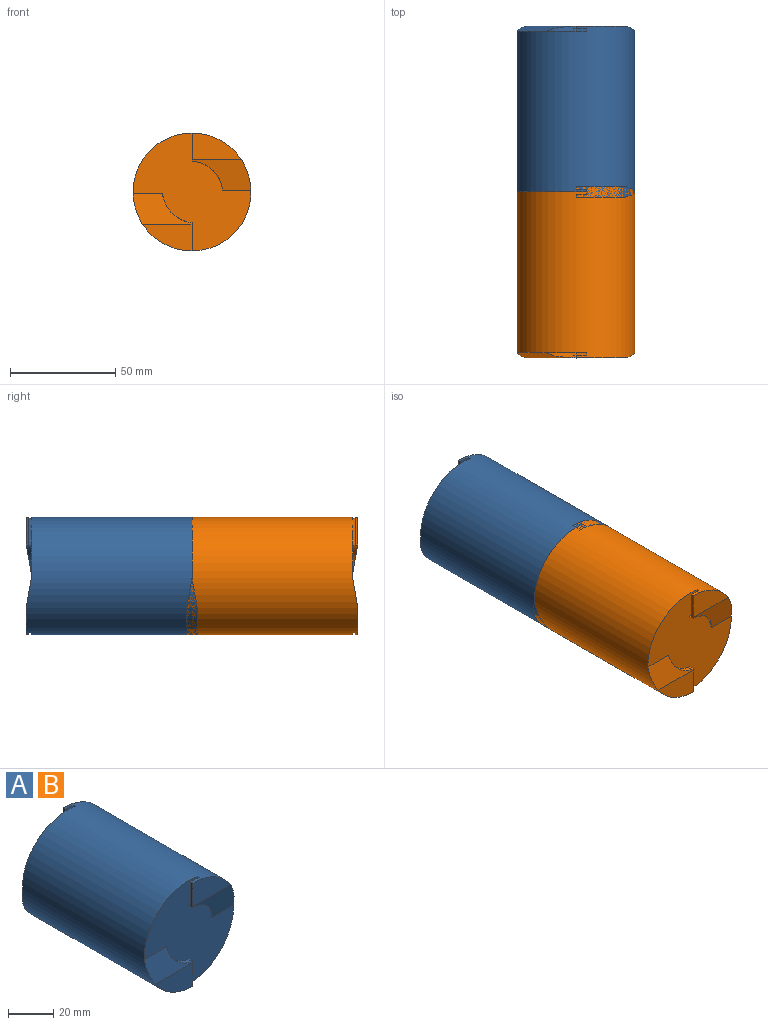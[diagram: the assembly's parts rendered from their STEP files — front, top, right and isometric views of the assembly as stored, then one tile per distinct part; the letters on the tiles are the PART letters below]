
ASSEMBLY  parts=2 mates=1
PART A: 31 faces, bbox 55.9x81.3x55.9 mm
  f0: plane 13.39x1.33mm, normal (1,0,0), area 17.7mm2, adj f1,f6,f7,f9,f14
  f1: cylinder r=27.97mm len=81.28mm, axis (0,1,0), area 13724mm2, adj f0,f2,f3,f5,f7,f8,f9,f10
  f2: plane 13.39x1.27mm, normal (-1,0,0), area 17mm2, adj f1,f4,f5,f8,f11
  f3: plane 55.95x55.95mm, normal (0,-1,0), area 1735.2mm2, adj f1,f4,f6,f8,f9,f10,f12,f13
  f4: cylinder r=15.37mm len=14.52mm, axis (0,1,0), area 33.2mm2, adj f2,f3,f8,f12
  f5: plane 23.46x12.73mm, normal (0,-1,0), area 210.4mm2, adj f1,f2,f8
  f6: cylinder r=15.76mm len=14.01mm, axis (0,1,0), area 31.7mm2, adj f0,f3,f9,f15
  f7: plane 23.46x12.73mm, normal (0,-1,0), area 210.4mm2, adj f0,f1,f9
  f8: plane 27.96x14.41mm, normal (0,-0.98,-0.17), area 233.9mm2, adj f1,f2,f3,f4,f5
  f9: plane 27.96x14.41mm, normal (0,-0.98,0.17), area 242.2mm2, adj f0,f1,f3,f6,f7
  f10: plane 12.92x1.27mm, normal (-1,0,0), area 16.4mm2, adj f1,f3,f11,f12
  f11: plane 13.39x5.08mm, normal (0,1,0), area 67.2mm2, adj f1,f2,f10,f12
  f12: plane 5.08x1.27mm, normal (0,0,1), area 6.5mm2, adj f3,f4,f10,f11
  f13: plane 12.33x1.21mm, normal (1,0,0), area 14.9mm2, adj f1,f3,f14,f15
  f14: plane 13.39x7.62mm, normal (0,1,0), area 99.3mm2, adj f0,f1,f13,f15
  f15: plane 7.62x1.21mm, normal (0,0,-1), area 9.2mm2, adj f3,f6,f13,f14
  f16: plane 13.39x1.33mm, normal (1,0,0), area 17.7mm2, adj f1,f21,f22,f24,f29
  f17: plane 13.39x1.27mm, normal (-1,0,0), area 17mm2, adj f1,f19,f20,f23,f26
  f18: plane 55.95x55.95mm, normal (0,1,0), area 1735.2mm2, adj f1,f19,f21,f23,f24,f25,f27,f28
  f19: cylinder r=15.37mm len=14.52mm, axis (0,-1,0), area 33.2mm2, adj f17,f18,f23,f27
  f20: plane 23.46x12.73mm, normal (0,1,0), area 210.4mm2, adj f1,f17,f23
  f21: cylinder r=15.76mm len=14.01mm, axis (0,-1,0), area 31.7mm2, adj f16,f18,f24,f30
  f22: plane 23.46x12.73mm, normal (0,1,0), area 210.4mm2, adj f1,f16,f24
  f23: plane 27.96x14.41mm, normal (0,0.98,-0.17), area 233.9mm2, adj f1,f17,f18,f19,f20
  f24: plane 27.96x14.41mm, normal (0,0.98,0.17), area 242.2mm2, adj f1,f16,f18,f21,f22
  f25: plane 12.92x1.27mm, normal (-1,0,0), area 16.4mm2, adj f1,f18,f26,f27
  f26: plane 13.39x5.08mm, normal (0,-1,0), area 67.2mm2, adj f1,f17,f25,f27
  f27: plane 5.08x1.27mm, normal (0,0,1), area 6.5mm2, adj f18,f19,f25,f26
  f28: plane 12.33x1.21mm, normal (1,0,0), area 14.9mm2, adj f1,f18,f29,f30
  f29: plane 13.39x7.62mm, normal (0,-1,0), area 99.3mm2, adj f1,f16,f28,f30
  f30: plane 7.62x1.21mm, normal (0,0,-1), area 9.2mm2, adj f18,f21,f28,f29
PART B: same geometry as A
PLACE A t=(-103.09,63.54,4.67)mm
PLACE B t=(-103.09,-12.66,4.67)mm
MATE fastened B.f1 <-> A.f1  axis (0,1,0) through (-103.09,25.44,4.67)mm
